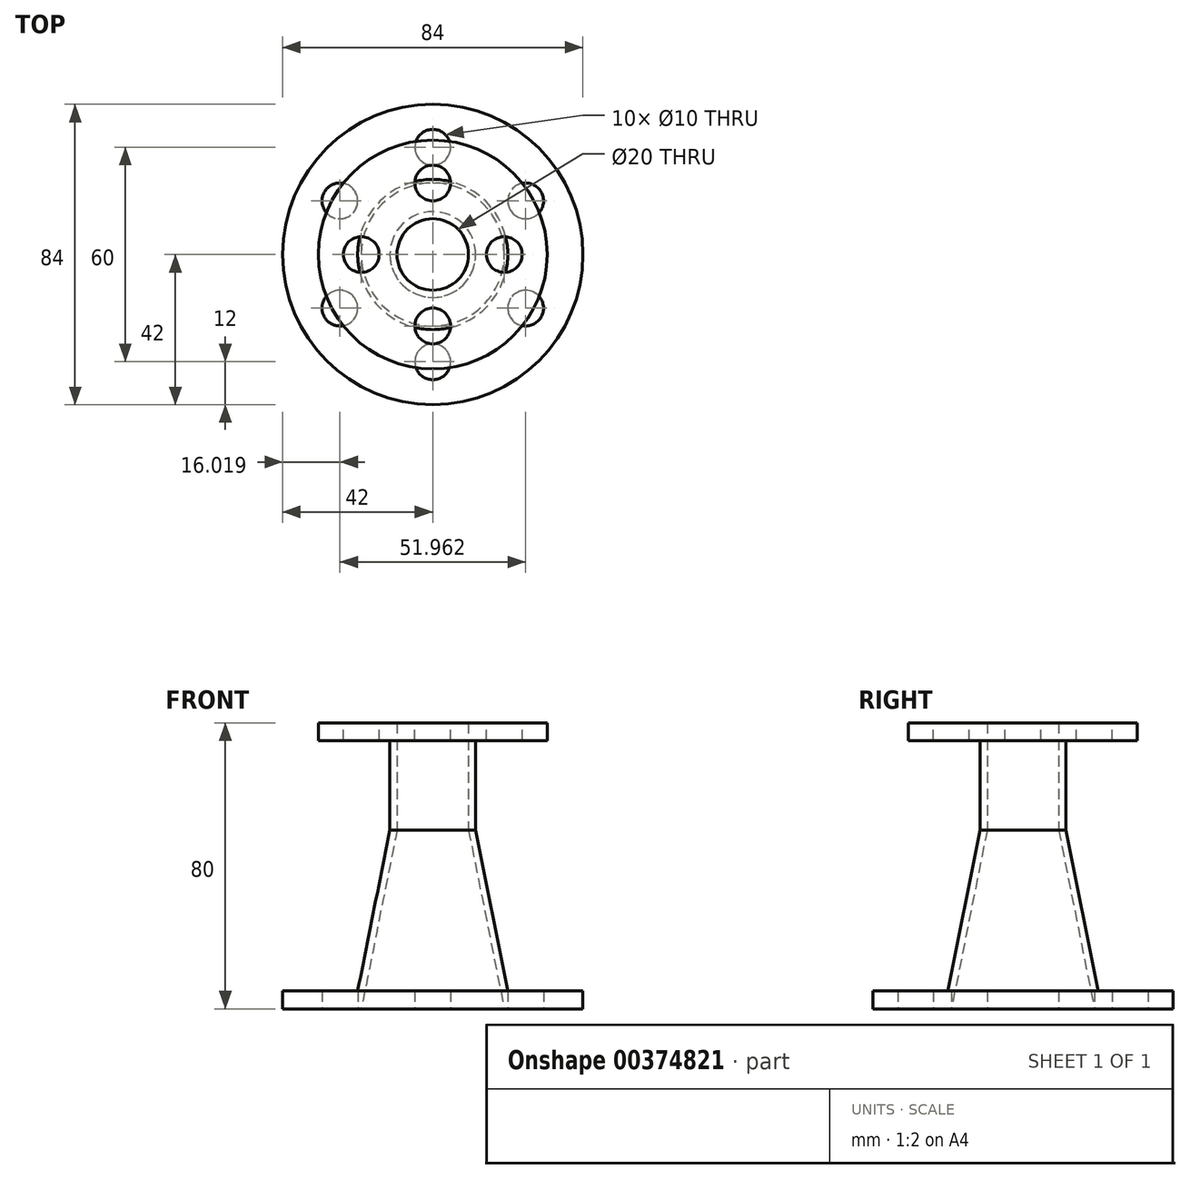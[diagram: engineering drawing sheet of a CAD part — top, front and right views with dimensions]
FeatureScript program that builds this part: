
annotation { "Feature Type Name" : "Feature", "Feature Type Description" : "" }
export const myFeature = defineFeature(function(context is Context, id is Id, definition is map)
    precondition{}
    {
        {
            var Q0;
            Q0=qCreatedBy(makeId("Top.planeOp"),FACE);
            var sketch = newSketch(context, id + "F0", { "sketchPlane" : qUnion([Q0])});
            skCircle(sketch, "E0", {"center": v(0, 0) * mm, "radius": 22 * mm});
            skSolve(sketch);
        }
        {
            var Q0;
            Q0=qCreatedBy(makeId("Top.planeOp"),FACE);
            cPlane(context, id + "F1", {"entities" : qUnion([Q0]), "cplaneType" : CPlaneType.OFFSET, "offset" : 50 * mm, "width" : 150 * mm, "height" : 150 * mm});
        }
        {
            var Q0;
            Q0=qCreatedBy(id+"F1.planeOp",FACE);
            var sketch = newSketch(context, id + "F2", { "sketchPlane" : qUnion([Q0])});
            skCircle(sketch, "E1", {"center": v(0, 0) * mm, "radius": 12 * mm});
            skSolve(sketch);
        }
        {
            var Q0;
            Q0=makeQuery(id+"F2.imprint","IMPRINT",FACE,{"disambiguationData":[TD([[makeQuery(id+"F2.imprint","IMPRINT",EDGE,{"derivedFrom":sQuery(id+"F2.wireOp",EDGE,"E1")}),1.0]])]});
            var Q1;
            Q1=makeQuery(id+"F0.imprint","IMPRINT",FACE,{"disambiguationData":[TD([[makeQuery(id+"F0.imprint","IMPRINT",EDGE,{"derivedFrom":sQuery(id+"F0.wireOp",EDGE,"E0")}),1.0]])]});
            loft(context, id + "F3", {"sheetProfilesArray" : [{ "sheetProfileEntities" : qUnion([Q0]) }, { "sheetProfileEntities" : qUnion([Q1]) }]});
        }
        {
            var Q0;
            Q0=makeQuery(id+"F3.opLoft","CAP_FACE",FACE,{"disambiguationData":[OSD([makeQuery(id+"F2.imprint","IMPRINT",FACE,{"disambiguationData":[TD([[makeQuery(id+"F2.imprint","IMPRINT",EDGE,{"derivedFrom":sQuery(id+"F2.wireOp",EDGE,"E1")}),1.0]])]})])],"isStart":true});
            var sketch = newSketch(context, id + "F4", { "sketchPlane" : qUnion([Q0])});
            skCircle(sketch, "E2", {"center": v(0, 0) * mm, "radius": 10 * mm});
            skSolve(sketch);
        }
        {
            var Q0;
            Q0=makeQuery(id+"F3.opLoft","CAP_FACE",FACE,{"disambiguationData":[OSD([makeQuery(id+"F0.imprint","IMPRINT",FACE,{"disambiguationData":[TD([[makeQuery(id+"F0.imprint","IMPRINT",EDGE,{"derivedFrom":sQuery(id+"F0.wireOp",EDGE,"E0")}),1.0]])]})])],"isStart":true});
            var sketch = newSketch(context, id + "F5", { "sketchPlane" : qUnion([Q0])});
            skCircle(sketch, "E3", {"center": v(0, 0) * mm, "radius": 20 * mm});
            skSolve(sketch);
        }
        {
            var Q0;
            Q0=makeQuery(id+"F5.imprint","IMPRINT",FACE,{"disambiguationData":[TD([[makeQuery(id+"F5.imprint","IMPRINT",EDGE,{"derivedFrom":sQuery(id+"F5.wireOp",EDGE,"E3")}),1.0]])]});
            var sketch = newSketch(context, id + "F6", { "sketchPlane" : qUnion([Q0])});
            skCircle(sketch, "E4", {"center": v(0, 0) * mm, "radius": 42 * mm});
            skSolve(sketch);
        }
        {
            var Q0;
            Q0=makeQuery(id+"F6.imprint","IMPRINT",FACE,{"disambiguationData":[TD([[makeQuery(id+"F6.imprint","IMPRINT",EDGE,{"derivedFrom":sQuery(id+"F6.wireOp",EDGE,"E4")}),1.0]])]});
            extrude(context, id + "F7", {"entities" : qUnion([Q0]), "operationType" : NewBodyOperationType.ADD, "oppositeDirection" : true, "depth" : 5 * mm});
        }
        {
            var Q1;
            Q1=makeQuery(id+"F5.imprint","IMPRINT",FACE,{"disambiguationData":[TD([[makeQuery(id+"F5.imprint","IMPRINT",EDGE,{"derivedFrom":sQuery(id+"F5.wireOp",EDGE,"E3")}),1.0]])]});
            var Q2;
            Q2=makeQuery(id+"F4.imprint","IMPRINT",FACE,{"disambiguationData":[TD([[makeQuery(id+"F4.imprint","IMPRINT",EDGE,{"derivedFrom":sQuery(id+"F4.wireOp",EDGE,"E2")}),1.0]])]});
            loft(context, id + "F8", {"operationType" : NewBodyOperationType.REMOVE, "sheetProfilesArray" : [{ "sheetProfileEntities" : qUnion([Q1]) }, { "sheetProfileEntities" : qUnion([Q2]) }]});
        }
        {
            var Q0;
            Q0=makeQuery(id+"F7.boolean.opBoolean","MERGE",FACE,{"derivedFrom":[makeQuery(id+"F3.opLoft","CAP_FACE",FACE,{"disambiguationData":[OSD([makeQuery(id+"F0.imprint","IMPRINT",FACE,{"disambiguationData":[TD([[makeQuery(id+"F0.imprint","IMPRINT",EDGE,{"derivedFrom":sQuery(id+"F0.wireOp",EDGE,"E0")}),1.0]])]})])],"isStart":true}),makeQuery(id+"F7.opExtrude","CAP_FACE",FACE,{"disambiguationData":[OSD([sQuery(id+"F5.wireOp",EDGE,"E3"),sQuery(id+"F6.wireOp",EDGE,"E4")])],"isStart":true})]});
            var sketch = newSketch(context, id + "F9", { "sketchPlane" : qUnion([Q0])});
            skCircle(sketch, "E5", {"center": v(0, 30) * mm, "radius": 5 * mm});
            skCircle(sketch, "E6.1.0", {"center": v(-25.98, 15) * mm, "radius": 5 * mm});
            skCircle(sketch, "E6.2.0", {"center": v(-25.98, -15) * mm, "radius": 5 * mm});
            skPoint(sketch, "E6.center", {"position": v(0, 0) * mm});
            skCircle(sketch, "E7.1.3.0", {"center": v(0, -30) * mm, "radius": 5 * mm});
            skCircle(sketch, "E7.1.4.0", {"center": v(25.98, -15) * mm, "radius": 5 * mm});
            skCircle(sketch, "E7.1.5.0", {"center": v(25.98, 15) * mm, "radius": 5 * mm});
            skSolve(sketch);
        }
        {
            var Q0;
            Q0=makeQuery(id+"F9.imprint","IMPRINT",FACE,{"disambiguationData":[TD([[makeQuery(id+"F9.imprint","IMPRINT",EDGE,{"derivedFrom":sQuery(id+"F9.wireOp",EDGE,"E5")}),1.0]])]});
            var Q1;
            Q1=makeQuery(id+"F9.imprint","IMPRINT",FACE,{"disambiguationData":[TD([[makeQuery(id+"F9.imprint","IMPRINT",EDGE,{"derivedFrom":sQuery(id+"F9.wireOp",EDGE,"E6.1.0")}),1.0]])]});
            var Q2;
            Q2=makeQuery(id+"F9.imprint","IMPRINT",FACE,{"disambiguationData":[TD([[makeQuery(id+"F9.imprint","IMPRINT",EDGE,{"derivedFrom":sQuery(id+"F9.wireOp",EDGE,"E7.1.5.0")}),1.0]])]});
            var Q3;
            Q3=makeQuery(id+"F9.imprint","IMPRINT",FACE,{"disambiguationData":[TD([[makeQuery(id+"F9.imprint","IMPRINT",EDGE,{"derivedFrom":sQuery(id+"F9.wireOp",EDGE,"E7.1.4.0")}),1.0]])]});
            var Q4;
            Q4=makeQuery(id+"F9.imprint","IMPRINT",FACE,{"disambiguationData":[TD([[makeQuery(id+"F9.imprint","IMPRINT",EDGE,{"derivedFrom":sQuery(id+"F9.wireOp",EDGE,"E7.1.3.0")}),1.0]])]});
            var Q5;
            Q5=makeQuery(id+"F9.imprint","IMPRINT",FACE,{"disambiguationData":[TD([[makeQuery(id+"F9.imprint","IMPRINT",EDGE,{"derivedFrom":sQuery(id+"F9.wireOp",EDGE,"E6.2.0")}),1.0]])]});
            var Q6;
            Q6=makeQuery(id+"F7.opExtrude","CAP_FACE",FACE,{"disambiguationData":[OSD([sQuery(id+"F5.wireOp",EDGE,"E3"),sQuery(id+"F6.wireOp",EDGE,"E4")])],"isStart":false});
            extrude(context, id + "F10", {"entities" : qUnion([Q0, Q1, Q2, Q3, Q4, Q5]), "operationType" : NewBodyOperationType.REMOVE, "endBound" : BoundingType.UP_TO_SURFACE, "oppositeDirection" : true, "endBoundEntityFace" : qUnion([Q6]), "depth" : 25 * mm});
        }
        {
            var Q0;
            Q0=makeQuery(id+"F4.imprint","IMPRINT",FACE,{"disambiguationData":[TD([[makeQuery(id+"F4.imprint","IMPRINT",EDGE,{"derivedFrom":sQuery(id+"F4.wireOp",EDGE,"E2")}),-1.0]])]});
            extrude(context, id + "F11", {"entities" : qUnion([Q0]), "operationType" : NewBodyOperationType.ADD, "depth" : 30 * mm});
        }
        {
            var Q0;
            Q0=makeQuery(id+"F11.opExtrude","CAP_FACE",FACE,{"disambiguationData":[OSD([sQuery(id+"F2.wireOp",EDGE,"E1"),sQuery(id+"F4.wireOp",EDGE,"E2")])],"isStart":false});
            var sketch = newSketch(context, id + "F12", { "sketchPlane" : qUnion([Q0])});
            skCircle(sketch, "E8", {"center": v(0, 0) * mm, "radius": 32 * mm});
            skSolve(sketch);
        }
        {
            var Q0;
            Q0=makeQuery(id+"F12.imprint","IMPRINT",FACE,{"disambiguationData":[TD([[makeQuery(id+"F12.imprint","IMPRINT",EDGE,{"derivedFrom":sQuery(id+"F12.wireOp",EDGE,"E8")}),1.0]])]});
            extrude(context, id + "F13", {"entities" : qUnion([Q0]), "operationType" : NewBodyOperationType.ADD, "oppositeDirection" : true, "depth" : 5 * mm});
        }
        {
            var Q0;
            {var subQ0=sQuery(id+"F2.wireOp",EDGE,"E1");Q0=makeQuery(id+"F13.boolean.opBoolean","MERGE",FACE,{"derivedFrom":[makeQuery(id+"F11.opExtrude","CAP_FACE",FACE,{"disambiguationData":[OSD([subQ0,sQuery(id+"F4.wireOp",EDGE,"E2")])],"isStart":false}),makeQuery(id+"F13.opExtrude","CAP_FACE",FACE,{"disambiguationData":[OSD([subQ0,sQuery(id+"F12.wireOp",EDGE,"E8")])],"isStart":true})]});}
            var sketch = newSketch(context, id + "F14", { "sketchPlane" : qUnion([Q0])});
            skCircle(sketch, "E9", {"center": v(0, 20) * mm, "radius": 5 * mm});
            skCircle(sketch, "E10.1.0", {"center": v(-20, 0) * mm, "radius": 5 * mm});
            skCircle(sketch, "E10.2.0", {"center": v(0, -20) * mm, "radius": 5 * mm});
            skPoint(sketch, "E10.center", {"position": v(0, 0) * mm});
            skCircle(sketch, "E11.1.3.0", {"center": v(20, 0) * mm, "radius": 5 * mm});
            skSolve(sketch);
        }
        {
            var Q0;
            Q0 = qSketchRegion(id + "F14", true);
            var Q1;
            Q1=makeQuery(id+"F13.opExtrude","CAP_FACE",FACE,{"disambiguationData":[OSD([sQuery(id+"F2.wireOp",EDGE,"E1"),sQuery(id+"F12.wireOp",EDGE,"E8")])],"isStart":false});
            extrude(context, id + "F15", {"entities" : qUnion([Q0]), "operationType" : NewBodyOperationType.REMOVE, "endBound" : BoundingType.UP_TO_SURFACE, "oppositeDirection" : true, "endBoundEntityFace" : qUnion([Q1]), "depth" : 25 * mm});
        }
    });
